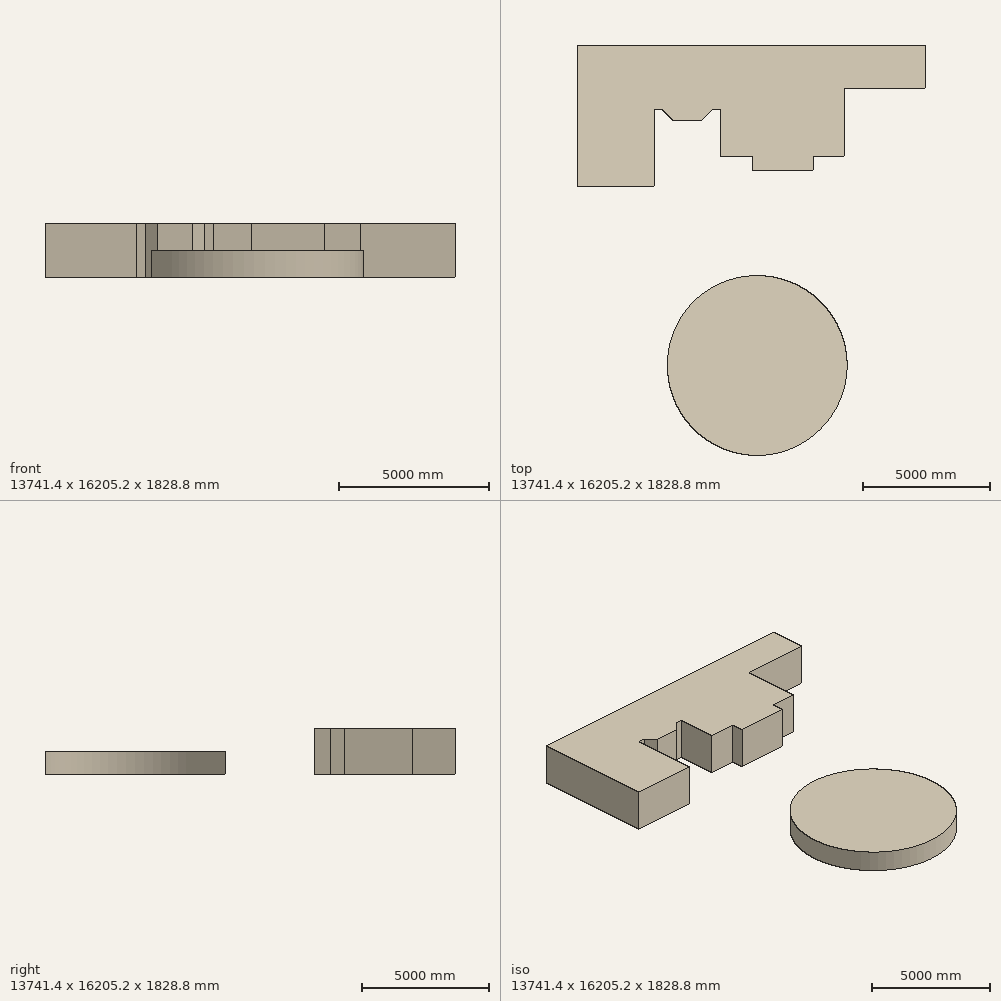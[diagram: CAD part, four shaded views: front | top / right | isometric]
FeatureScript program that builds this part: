
annotation { "Feature Type Name" : "Feature", "Feature Type Description" : "" }
export const myFeature = defineFeature(function(context is Context, id is Id, definition is map)
    precondition{}
    {
        {
            var Q0;
            Q0=qCreatedBy(makeId("Top.planeOp"),FACE);
            var sketch = newSketch(context, id + "F0", { "sketchPlane" : qUnion([Q0])});
            skLineSegment(sketch, "E0", {"start": v(0, 0) * mm, "end": v(0, -5588) * mm});
            skLineSegment(sketch, "E1", {"start": v(0, -5588) * mm, "end": v(3048, -5588) * mm});
            skLineSegment(sketch, "E2", {"start": v(3048, -5588) * mm, "end": v(3048, -2540) * mm});
            skLineSegment(sketch, "E3", {"start": v(3048, -2540) * mm, "end": v(3352.8, -2540) * mm});
            skLineSegment(sketch, "E4", {"start": v(3352.8, -2540) * mm, "end": v(3759.2, -2946.4) * mm});
            skLineSegment(sketch, "E5", {"start": v(3759.2, -2946.4) * mm, "end": v(4914.9, -2946.4) * mm});
            skLineSegment(sketch, "E6", {"start": v(4914.9, -2946.4) * mm, "end": v(5321.3, -2540) * mm});
            skLineSegment(sketch, "E7", {"start": v(5321.3, -2540) * mm, "end": v(5626.1, -2540) * mm});
            skLineSegment(sketch, "E8", {"start": v(5626.1, -2540) * mm, "end": v(5626.1, -4368.8) * mm});
            skLineSegment(sketch, "E9", {"start": v(5626.1, -4368.8) * mm, "end": v(6896.1, -4368.8) * mm});
            skLineSegment(sketch, "E10", {"start": v(6896.1, -4368.8) * mm, "end": v(6896.1, -4927.6) * mm});
            skLineSegment(sketch, "E11", {"start": v(6896.1, -4927.6) * mm, "end": v(9334.5, -4927.6) * mm});
            skLineSegment(sketch, "E12", {"start": v(9334.5, -4927.6) * mm, "end": v(9334.5, -4368.8) * mm});
            skLineSegment(sketch, "E13", {"start": v(9334.5, -4368.8) * mm, "end": v(10553.7, -4368.8) * mm});
            skLineSegment(sketch, "E14", {"start": v(10553.7, -4368.8) * mm, "end": v(10553.7, -1680.39) * mm});
            skLineSegment(sketch, "E15", {"start": v(10553.7, -1680.39) * mm, "end": v(13741.4, -1680.39) * mm});
            skLineSegment(sketch, "E16", {"start": v(13741.4, -1680.39) * mm, "end": v(13741.4, 0) * mm});
            skLineSegment(sketch, "E17", {"start": v(13741.4, 0) * mm, "end": v(0, 0) * mm});
            skSolve(sketch);
        }
        {
            var Q0;
            Q0=makeQuery(id+"F0.imprint","IMPRINT",FACE,{"disambiguationData":[TD([[makeQuery(id+"F0.imprint","IMPRINT",EDGE,{"derivedFrom":sQuery(id+"F0.wireOp",EDGE,"E0")}),1.0]])]});
            extrude(context, id + "F1", {"entities" : qUnion([Q0]), "depth" : 1828.8 * mm});
        }
        {
            var Q0;
            Q0=qCreatedBy(makeId("Top.planeOp"),FACE);
            var sketch = newSketch(context, id + "F2", { "sketchPlane" : qUnion([Q0])});
            skCircle(sketch, "E18", {"center": v(7099.3, -12649.2) * mm, "radius": 3556 * mm});
            skSolve(sketch);
        }
        {
            var Q0;
            Q0=makeQuery(id+"F2.imprint","IMPRINT",FACE,{"disambiguationData":[TD([[makeQuery(id+"F2.imprint","IMPRINT",EDGE,{"derivedFrom":sQuery(id+"F2.wireOp",EDGE,"E18")}),1.0]])]});
            extrude(context, id + "F3", {"entities" : qUnion([Q0]), "depth" : 914.4 * mm});
        }
    });
